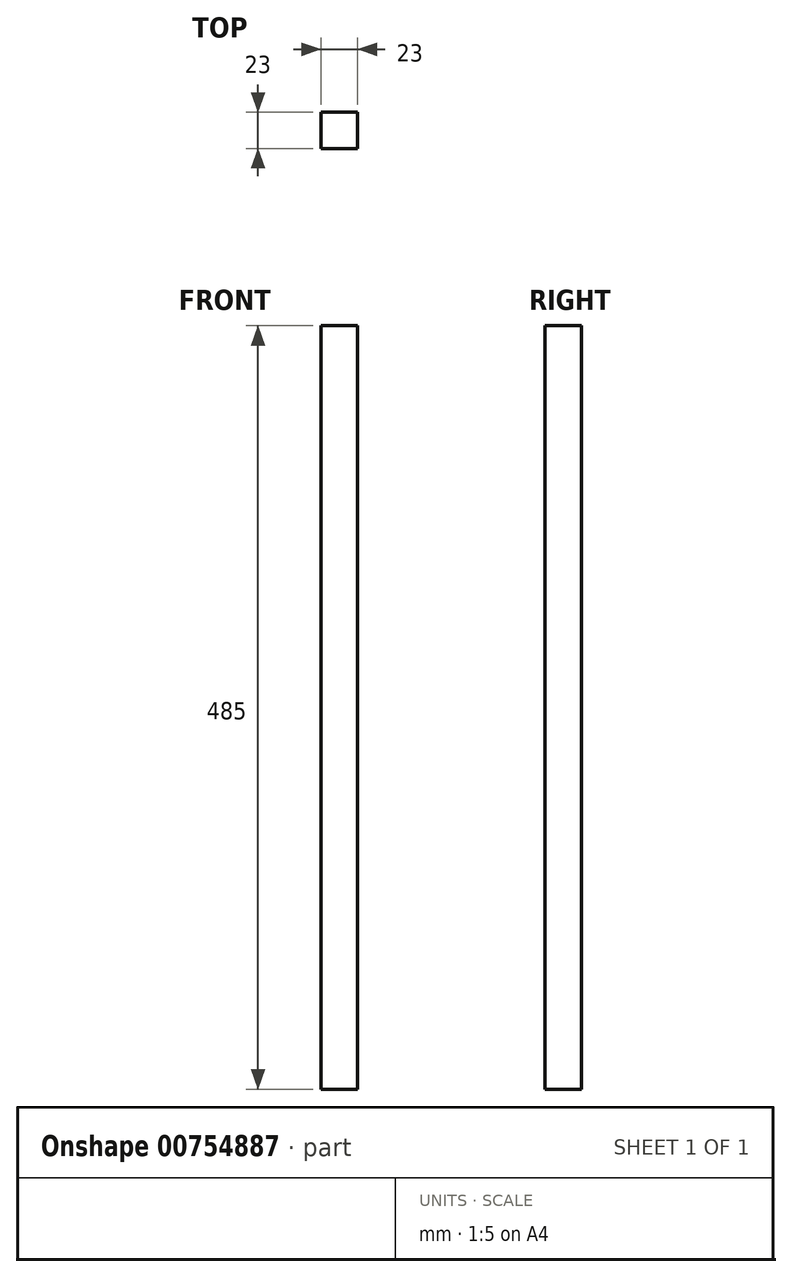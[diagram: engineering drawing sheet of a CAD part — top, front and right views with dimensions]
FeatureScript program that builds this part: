
annotation { "Feature Type Name" : "Feature", "Feature Type Description" : "" }
export const myFeature = defineFeature(function(context is Context, id is Id, definition is map)
    precondition{}
    {
        {
            var Q0;
            Q0=qCreatedBy(makeId("Top.planeOp"),FACE);
            var sketch = newSketch(context, id + "F0", { "sketchPlane" : qUnion([Q0])});
            skLineSegment(sketch, "E0.bottom", {"start": v(-11.5, 11.5) * mm, "end": v(11.5, 11.5) * mm});
            skLineSegment(sketch, "E0.top", {"start": v(-11.5, -11.5) * mm, "end": v(11.5, -11.5) * mm});
            skLineSegment(sketch, "E0.left", {"start": v(-11.5, 11.5) * mm, "end": v(-11.5, -11.5) * mm});
            skLineSegment(sketch, "E0.right", {"start": v(11.5, 11.5) * mm, "end": v(11.5, -11.5) * mm});
            skPoint(sketch, "E0.middle", {"position": v(0, 0) * mm});
            skSolve(sketch);
        }
        {
            var Q0;
            Q0 = qSketchRegion(id + "F0", true);
            extrude(context, id + "F1", {"entities" : qUnion([Q0]), "depth" : 485 * mm, "offsetDistance" : 25 * mm});
        }
    });
